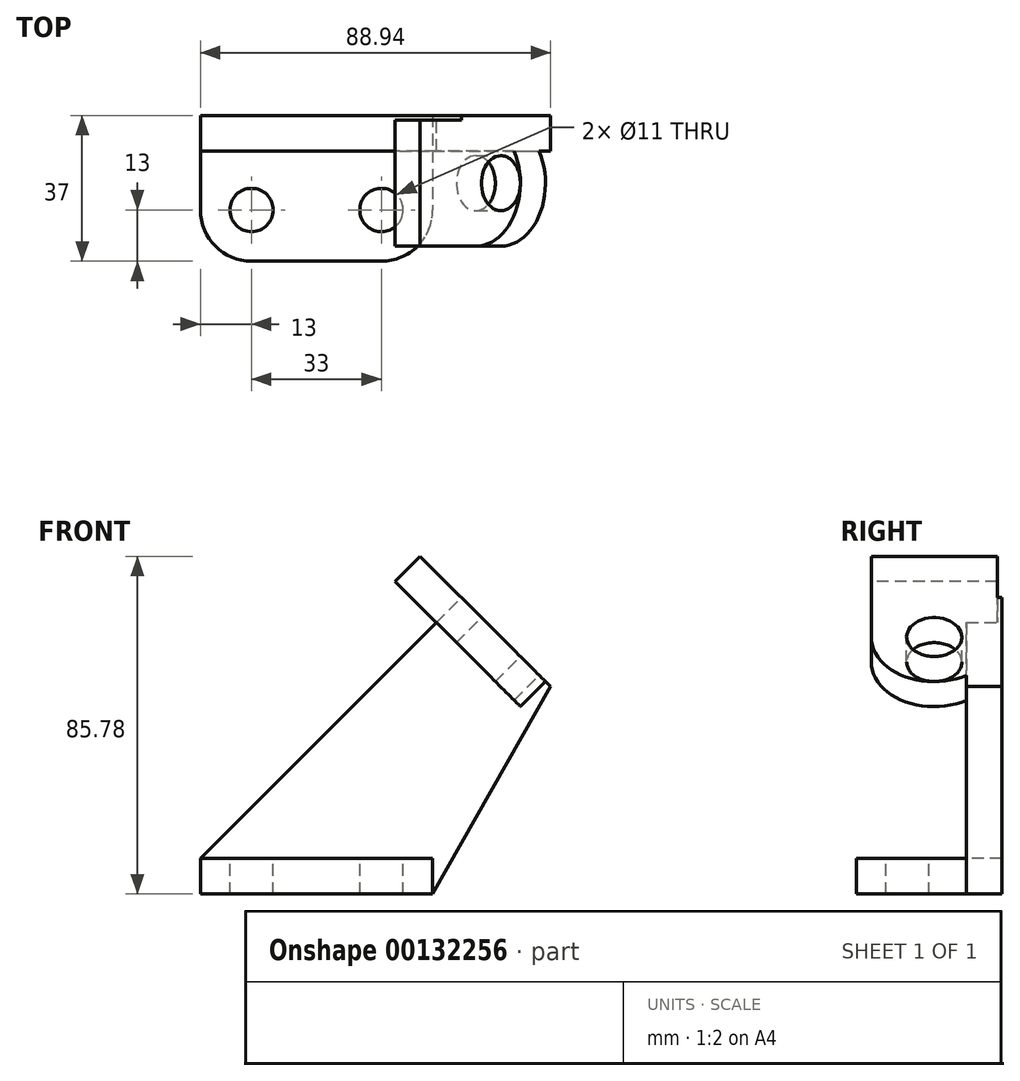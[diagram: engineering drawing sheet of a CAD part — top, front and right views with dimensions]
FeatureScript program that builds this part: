
annotation { "Feature Type Name" : "Feature", "Feature Type Description" : "" }
export const myFeature = defineFeature(function(context is Context, id is Id, definition is map)
    precondition{}
    {
        {
            var Q0;
            Q0=qCreatedBy(makeId("Top.planeOp"),FACE);
            var sketch = newSketch(context, id + "F0", { "sketchPlane" : qUnion([Q0])});
            skCircle(sketch, "E0", {"center": v(0, 0) * mm, "radius": 5.5 * mm});
            skCircle(sketch, "E1", {"center": v(33, 0) * mm, "radius": 5.5 * mm});
            skLineSegment(sketch, "E2.bottom", {"start": v(-13, 24) * mm, "end": v(46, 24) * mm});
            skLineSegment(sketch, "E2.top", {"start": v(0, -13) * mm, "end": v(33, -13) * mm});
            skLineSegment(sketch, "E2.left", {"start": v(-13, 24) * mm, "end": v(-13, 0) * mm});
            skLineSegment(sketch, "E2.right", {"start": v(46, 24) * mm, "end": v(46, 0) * mm});
            skPoint(sketch, "E3.visualSharp", {"position": v(-13, -13) * mm});
            skArc(sketch, "E3.filletArc", {"start": v(-13, 0) * mm, "mid": v(-9.2, -9.2) * mm, "end": v(0, -13) * mm});
            skPoint(sketch, "E4.visualSharp", {"position": v(46, -13) * mm});
            skArc(sketch, "E4.filletArc", {"start": v(33, -13) * mm, "mid": v(42.2, -9.2) * mm, "end": v(46, 0) * mm});
            skSolve(sketch);
        }
        {
            var Q0;
            Q0=makeQuery(id+"F0.imprint","IMPRINT",FACE,{"disambiguationData":[TD([[makeQuery(id+"F0.imprint","IMPRINT",EDGE,{"derivedFrom":sQuery(id+"F0.wireOp",EDGE,"E0")}),-1.0]])]});
            extrude(context, id + "F1", {"entities" : qUnion([Q0]), "oppositeDirection" : true, "depth" : 9 * mm});
        }
        {
            var Q0;
            Q0=makeQuery(id+"F1.opExtrude","SWEPT_FACE",FACE,{"disambiguationData":[OSD([sQuery(id+"F0.wireOp",EDGE,"E2.bottom")])]});
            var sketch = newSketch(context, id + "F2", { "sketchPlane" : qUnion([Q0])});
            skLineSegment(sketch, "E5", {"start": v(-46, -9) * mm, "end": v(-75.94, 43.69) * mm});
            skLineSegment(sketch, "E6", {"start": v(-75.94, 43.69) * mm, "end": v(-53.31, 66.31) * mm});
            skLineSegment(sketch, "E7", {"start": v(-53.31, 66.31) * mm, "end": v(13, 0) * mm});
            skPoint(sketch, "E8", {"position": v(-64.63, 55) * mm});
            skLineSegment(sketch, "E9", {"start": v(-64.63, 55) * mm, "end": v(-85.7, 55) * mm, "construction": true});
            skSolve(sketch);
        }
        {
            var Q0;
            Q0=makeQuery(id+"F2.imprint","IMPRINT",FACE,{"disambiguationData":[TD([[makeQuery(id+"F2.imprint","IMPRINT",EDGE,{"derivedFrom":sQuery(id+"F2.wireOp",EDGE,"E5")}),-1.0]])]});
            extrude(context, id + "F3", {"entities" : qUnion([Q0]), "operationType" : NewBodyOperationType.ADD, "oppositeDirection" : true, "depth" : 9 * mm});
        }
        {
            var Q0;
            Q0=makeQuery(id+"F3.opExtrude","SWEPT_FACE",FACE,{"disambiguationData":[OSD([sQuery(id+"F2.wireOp",EDGE,"E6")])]});
            var sketch = newSketch(context, id + "F4", { "sketchPlane" : qUnion([Q0])});
            skLineSegment(sketch, "E10.0", {"start": v(22.8, 24) * mm, "end": v(-9.2, 24) * mm});
            skLineSegment(sketch, "E11", {"start": v(-9.2, 24) * mm, "end": v(-9.2, -5) * mm});
            skLineSegment(sketch, "E12", {"start": v(22.8, 24) * mm, "end": v(22.8, -5) * mm});
            skCircle(sketch, "E13", {"center": v(6.8, -5) * mm, "radius": 7 * mm});
            skArc(sketch, "E14", {"start": v(-9.2, -5) * mm, "mid": v(6.8, -21) * mm, "end": v(22.8, -5) * mm});
            skSolve(sketch);
        }
        {
            var Q0;
            Q0=makeQuery(id+"F4.imprint","IMPRINT",FACE,{"disambiguationData":[TD([[makeQuery(id+"F4.imprint","IMPRINT",EDGE,{"derivedFrom":sQuery(id+"F4.wireOp",EDGE,"E13")}),-1.0]])]});
            extrude(context, id + "F5", {"entities" : qUnion([Q0]), "operationType" : NewBodyOperationType.ADD, "oppositeDirection" : true, "depth" : 9 * mm});
        }
    });
